# Revit family: Foundation-Barrier-Stego-Wrap-Vapor_Retarder
name_source: partatom
category: Specialty Equipment
units: mm (PartAtom-declared; Revit-internal decimal feet)

## family parameters
Cut with Voids When Loaded = No
Host = Face
OmniClass Number = 23.25.05.21
OmniClass Title = Special Foundations
Part Type = Normal
Room Calculation Point = No
Round Connector Dimension = Use Diameter
Shared = No

## types (2) — shared parameters
BIMobject category = Waterproofing & Membranes
Brand url = http://www.stegoindustries.com
Date of publishing = 8/16/2017
Default Elevation = 0' - 0"
Design country = United States
Edition number = 1
Installation instructions = https://www.stegoindustries.com
Low Emitting Material = Yes
Manufacturer = Stego Industries, LLC
Manufacturer country = United States
Manufacturer name = Stego Industries, LLC
Masterformat 2014 Code = 07 26 00
Masterformat 2014 Description = Vapor Retarders
Material main = Polyethylene
Max Length Note = Maximum roll length is 210'.
Nominal height = 0' - 0"
Nominal width = 0' - 0"
Product Documentation Link = https://www.stegoindustries.com
Product Guid = 90038d3d-66a8-4364-87c4-b1adead07e54
Product Page URL = https://www.stegoindustries.com
Product certification = https://www.stegoindustries.com
Product data url = https://bimobject.com
Product family = Thermal and Moisture Protective Products
Product group = Stego Wrap
Product url = https://www.stegoindustries.com
QR code = http://bimobject.com
Stego Vapor Barrier = Stego® Wrap Class C Vapor Retarder
Technical description = Under-Slab Vapor Retarder
URL = http://www.stegoindustries.com
Vapor Barrier Thickness = 10 mils
Weight Net (Kg) = 0
Youtube clip = https://www.youtube.com

## per-type parameters (varying)
| type | ASTM | Description | Model | Product SKU |
| Stego® Wrap Class A Vapor Retarder 10 mils | Exceeds ASTM E1745 Class A Requirements | Stego® Wrap Class A Vapor Retarder (10-mil) is an exceptional under-slab vapor retarder.  Stego Wrap Class A Vapor Retarder is a multi-layer plastic extrusion manufactured with only high grade prime, virgin, polyolefin resins. Stego Wrap Class A Vapor Retarder can be used in systems for the control of soil gases (radon, methane), soil poisons (oil by-products) and sulfates. | Stego® Wrap Class A Vapor Retarder (10 mils) | stego001 |
| Stego® Wrap Class C Vapor Retarder 10 mils | Meets ASTM E1745 Requirements | Stego® Wrap Class C Vapor Retarder (10-mil) is used as an exceptional vapor retarder, and as a protection course for below grade waterproofing applications.  Stego Wrap Class C Vapor Retarder is a multi-layer plastic extrusion manufactured with only the highest grade of prime, virgin, polyolefin resins. Stego Wrap Class C can be used in systems for the control of soil gases (radon, methane), soil poisons (oil by-products) and sulfates. Stego Wrap Class C Vapor Retarder exceeds the requirements of ASTM E1745 Class C and is engineered with a low permeance. | Stego® Wrap Class C Vapor Retarder (10 mils) | stego004 |

## geometry (parser evidence)
native form markers: Sweep x2
no freeform markers — native parametric forms only
